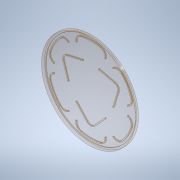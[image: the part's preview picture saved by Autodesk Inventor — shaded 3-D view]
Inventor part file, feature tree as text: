
AUTODESK INVENTOR PART (.ipt)
format: ipt  version: 2020 (Build 240168000, 168)  size: 399,360 bytes
history: native  units: in
note: dims shown in document units (in); Inventor stores cm internally (conversion verified against a paired STEP export)
features: sketch x14, extrude x11, projected_geometry x6, plane x2, shell x1, sweep x1, hole x1
ambient origin geometry x8: Origin, YZ Plane, XZ Plane, XY Plane, X Axis, Y Axis, Z Axis, Center Point
bodies: Solid1 (feature_tree)
feature tree (36):
  extrude  "Extrusion1"  Depth=3.1496in TaperAngle=0.0deg
  shell  "Shell1"  Thickness=0.1181in
  extrude  "Extrusion2"  Depth=3.1496in TaperAngle=0.0deg
  extrude  "Extrusion3"  Depth=1.5748in
  plane  "Work Plane1"
  extrude  "Extrusion4"  TaperAngle=120.0deg  [1 undecoded]
  extrude  "Extrusion5"  Depth=0.378in
  plane  "Work Plane4"
  sweep  "Sweep2"
  extrude  "Extrusion6"  [1 undecoded]
  hole  "Hole1"  [1 undecoded]
  extrude  "Extrusion9"  Depth=0.1181in TaperAngle=0.0deg
  extrude  "Extrusion10"  Depth=0.0591in
  extrude  "Extrusion11"  Depth=0.0591in
  extrude  "Extrusion13"  Depth=0.0591in
  extrude  "Extrusion12"  Depth=0.0591in
  sketch  "Sketch1"  dims[d1=5.3543in d2=3.1496in d3=0.0in d4=0.1181in]
  sketch  "Sketch2"  dims[d5=2.5197in d6=3.1496in d7=0.0in]
  sketch  "Sketch3"  dims[d8=0.378in d9=1.5748in]
  projected_geometry  "Projected Loop1"
  sketch  "Sketch4"  dims[d10=120.0deg d11=120.0deg]
  sketch  "Sketch6"  dims[d12=0.378in d13=0.378in]
  projected_geometry  "Projected Loop3"
  sketch  "Sketch9"  dims[d14=1.5748in d15=1.5748in]
  projected_geometry  "Projected Loop4"
  sketch  "Sketch10"  dims[d16=0.06in d17=0.0in d18=-0.9843in]
  sketch  "Sketch11"  dims[d24=1.1811in d25=0.9843in d26=0.0in]
  projected_geometry  "Projected Loop5"
  sketch  "Sketch14"  dims[d27=0.1181in d28=2.2201in d29=0.0in]
  sketch  "Sketch16"  dims[d37=0.0in d38=0.0in d39=0.0591in]
  sketch  "Sketch17"  dims[d40=0.0591in d41=0.0591in]
  projected_geometry  "Projected Loop7"
  sketch  "Sketch18"  dims[d42=0.0591in d43=0.0591in]
  sketch  "Sketch19"  dims[d44=0.0591in d45=0.0591in]
  sketch  "Sketch20"  dims[d46=0.9843in d47=0.9843in d48=0.9843in d49=0.9843in d50=0.9843in d51=0.9843in d52=0.0591in d53=0.0in d98=0.2362in d99=1.6142in d100=1.1811in d102=360.0deg d104=0.2362in d105=0.2362in d106=0.1575in d107=0.0787in d108=90.0deg d109=0.315in d110=0.8108in d111=0.3937in d112=0.0in d113=0.3937in d114=0.0in d115=5.5906in d116=0.378in d117=5.1181in d118=2.2638in d119=0.0591in d120=0.7874in d121=0.7874in d122=2.3622in d124=360.0deg d126=0.0591in d127=0.0591in d128=2.3622in d130=360.0deg d132=0.0591in d133=0.0in d134=0.378in d135=2.2638in d136=2.3622in d138=360.0deg d140=0.06in d141=0.0in d142=0.0591in d143=0.0in]
  projected_geometry  "Projected Loop8"
note: 3 required parameter values undecoded (feature->parameter linkage not recoverable at this tier; creation-order binding heuristic only, values carry confidence <= 0.55)
